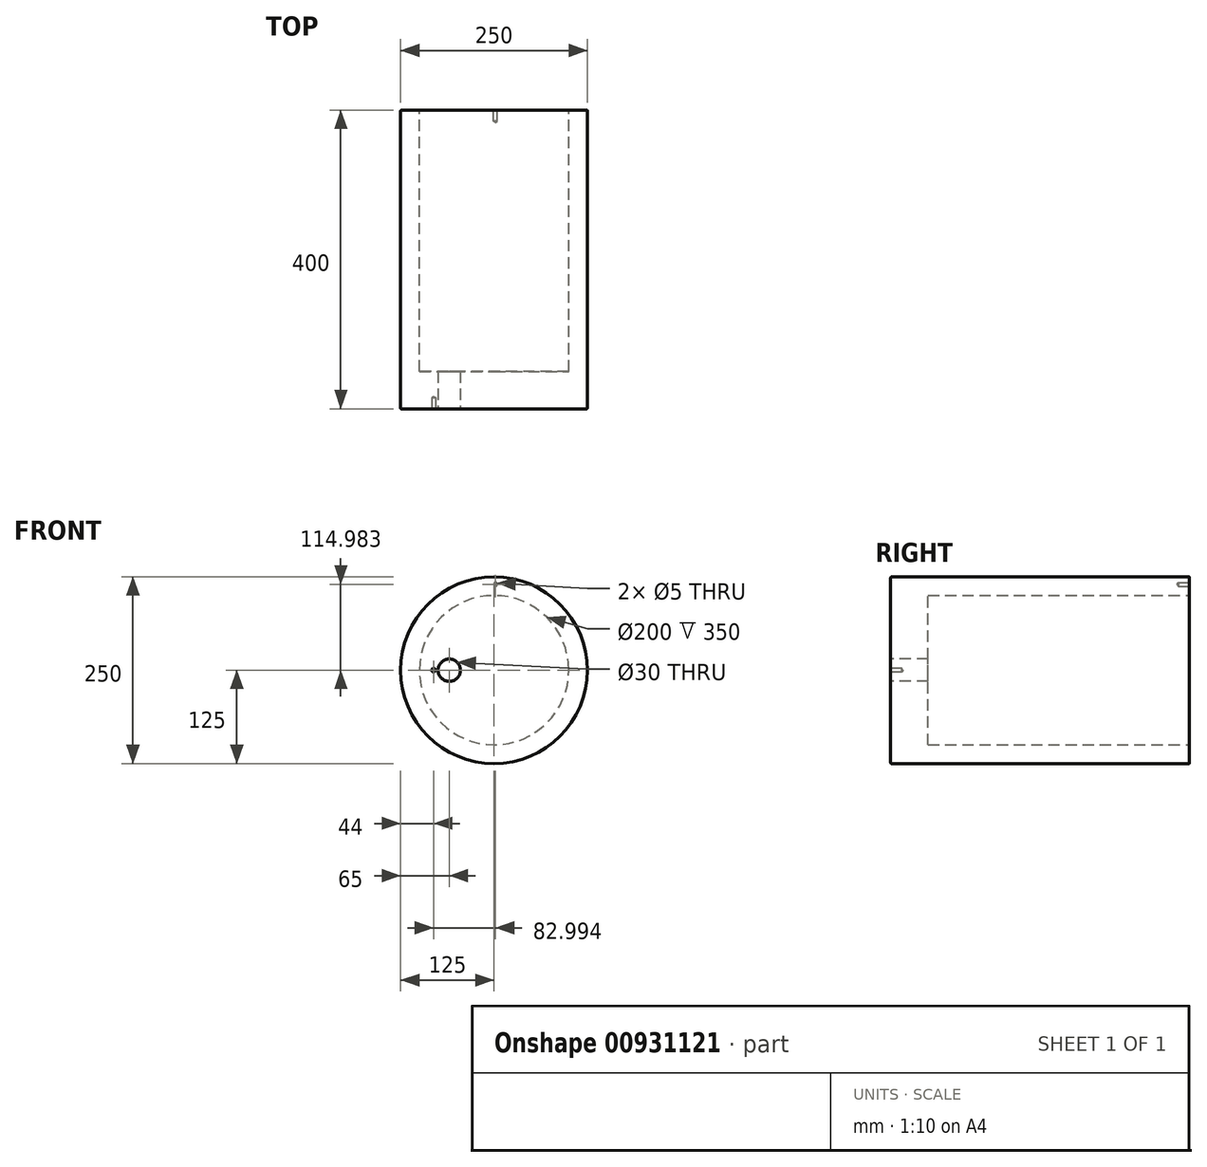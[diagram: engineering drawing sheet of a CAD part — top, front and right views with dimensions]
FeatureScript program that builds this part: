
annotation { "Feature Type Name" : "Feature", "Feature Type Description" : "" }
export const myFeature = defineFeature(function(context is Context, id is Id, definition is map)
    precondition{}
    {
        {
            var Q0;
            Q0=qCreatedBy(makeId("Front.planeOp"),FACE);
            var sketch = newSketch(context, id + "F0", { "sketchPlane" : qUnion([Q0])});
            skCircle(sketch, "E0", {"center": v(125, 0) * mm, "radius": 125 * mm});
            skSolve(sketch);
        }
        {
            var Q0;
            Q0=makeQuery(id+"F0.imprint","IMPRINT",FACE,{"disambiguationData":[TD([[makeQuery(id+"F0.imprint","IMPRINT",EDGE,{"derivedFrom":sQuery(id+"F0.wireOp",EDGE,"E0")}),1.0]])]});
            var Q1;
            Q1=sQuery(id+"F0.wireOp",EDGE,"E0");
            extrude(context, id + "F1", {"entities" : qUnion([Q0]), "surfaceEntities" : qUnion([Q1]), "depth" : 400 * mm, "offsetDistance" : 25 * mm});
        }
        {
            var Q0;
            Q0=makeQuery(id+"F0.imprint","IMPRINT",FACE,{"disambiguationData":[TD([[makeQuery(id+"F0.imprint","IMPRINT",EDGE,{"derivedFrom":sQuery(id+"F0.wireOp",EDGE,"E0")}),1.0]])]});
            var sketch = newSketch(context, id + "F2", { "sketchPlane" : qUnion([Q0])});
            skCircle(sketch, "E1", {"center": v(125, 0) * mm, "radius": 100 * mm});
            skSolve(sketch);
        }
        {
            var Q0;
            Q0=makeQuery(id+"F2.imprint","IMPRINT",FACE,{"disambiguationData":[TD([[makeQuery(id+"F2.imprint","IMPRINT",EDGE,{"derivedFrom":sQuery(id+"F2.wireOp",EDGE,"E1")}),1.0]])]});
            extrude(context, id + "F3", {"entities" : qUnion([Q0]), "operationType" : NewBodyOperationType.REMOVE, "depth" : 350 * mm, "offsetDistance" : 25 * mm});
        }
        {
            var Q0;
            Q0=makeQuery(id+"F1.opExtrude","CAP_EDGE",EDGE,{"disambiguationData":[OSD([sQuery(id+"F0.wireOp",EDGE,"E0")])],"isStart":true});
            var Q1;
            Q1=makeQuery(id+"F3.boolean.opBoolean","COPY",EDGE,{"derivedFrom":makeQuery(id+"F3.opExtrude","CAP_EDGE",EDGE,{"disambiguationData":[OSD([sQuery(id+"F2.wireOp",EDGE,"E1")])],"isStart":true})});
            var Q2;
            Q2=makeQuery(id+"F1.opExtrude","CAP_EDGE",EDGE,{"disambiguationData":[OSD([sQuery(id+"F0.wireOp",EDGE,"E0")])],"isStart":false});
            fillet(context, id + "F4", {"entities" : qUnion([Q0, Q1, Q2]), "radius" : 1 * mm, "tangentPropagation" : true, "allowEdgeOverflow" : false});
        }
        {
            var Q0;
            Q0=makeQuery(id+"F0.imprint","IMPRINT",FACE,{"disambiguationData":[TD([[makeQuery(id+"F0.imprint","IMPRINT",EDGE,{"derivedFrom":sQuery(id+"F0.wireOp",EDGE,"E0")}),1.0]])]});
            var sketch = newSketch(context, id + "F5", { "sketchPlane" : qUnion([Q0])});
            skPoint(sketch, "E2", {"position": v(127, 114.98) * mm});
            skSolve(sketch);
        }
        {
            var Q0;
            Q0=sQuery(id+"F5.wireOp",VERTEX,"E2");
            var Q1;
            Q1=makeQuery(id+"F1.opExtrude","SWEPT_BODY",BODY,{"disambiguationData":[OSD([sQuery(id+"F0.wireOp",EDGE,"E0")])]});
            hole(context, id + "F6", {"style" : HoleStyle.SIMPLE, "endStyle" : HoleEndStyle.BLIND, "oppositeDirection" : true, "standardTappedOrClearance" : lookupTablePath({ "standard" : "ISO", "engagement" : "75%", "pitch" : "1 mm", "size" : "M6", "type" : "Tapped" }), "standardBlindInLast" : lookupTablePath({ "standard" : "ISO", "fit" : "Normal", "engagement" : "75%", "pitch" : "1 mm", "size" : "M6", "type" : "Clearance & tapped" }), "holeDiameter" : 5 * mm, "majorDiameter" : 6 * mm, "showTappedDepth" : true, "holeDepth" : 15 * mm, "isTappedThrough" : true, "tappedDepth" : 12 * mm, "tapClearance" : 3, "startFromSketch" : true, "locations" : qUnion([Q0]), "scope" : qUnion([Q1])});
        }
        {
            var Q0;
            Q0=makeQuery(id+"F1.opExtrude","CAP_FACE",FACE,{"disambiguationData":[OSD([sQuery(id+"F0.wireOp",EDGE,"E0")])],"isStart":false});
            var sketch = newSketch(context, id + "F7", { "sketchPlane" : qUnion([Q0])});
            skPoint(sketch, "E3", {"position": v(65, 0) * mm});
            skSolve(sketch);
        }
        {
            var Q0;
            Q0=makeQuery(id+"F1.opExtrude","CAP_FACE",FACE,{"disambiguationData":[OSD([sQuery(id+"F0.wireOp",EDGE,"E0")])],"isStart":false});
            var sketch = newSketch(context, id + "F8", { "sketchPlane" : qUnion([Q0])});
            skPoint(sketch, "E4", {"position": v(44, 0) * mm});
            skSolve(sketch);
        }
        {
            var Q0;
            Q0=sQuery(id+"F7.wireOp",VERTEX,"E3");
            var Q1;
            Q1=makeQuery(id+"F1.opExtrude","SWEPT_BODY",BODY,{"disambiguationData":[OSD([sQuery(id+"F0.wireOp",EDGE,"E0")])]});
            hole(context, id + "F9", {"style" : HoleStyle.SIMPLE, "endStyle" : HoleEndStyle.THROUGH, "standardTappedOrClearance" : lookupTablePath({ "standard" : "ISO", "size" : "30", "type" : "Drilled" }), "standardBlindInLast" : lookupTablePath({ "standard" : "ISO", "size" : "30", "type" : "Drilled" }), "holeDiameter" : 30 * mm, "majorDiameter" : 5 * mm, "isTappedThrough" : true, "tappedDepth" : 12 * mm, "tapClearance" : 3, "startFromSketch" : true, "locations" : qUnion([Q0]), "scope" : qUnion([Q1])});
        }
        {
            var Q0;
            Q0=sQuery(id+"F8.wireOp",VERTEX,"E4");
            var Q1;
            Q1=makeQuery(id+"F1.opExtrude","SWEPT_BODY",BODY,{"disambiguationData":[OSD([sQuery(id+"F0.wireOp",EDGE,"E0")])]});
            hole(context, id + "F10", {"style" : HoleStyle.SIMPLE, "endStyle" : HoleEndStyle.BLIND, "standardTappedOrClearance" : lookupTablePath({ "standard" : "ISO", "engagement" : "75%", "pitch" : "1 mm", "size" : "M6", "type" : "Tapped" }), "standardBlindInLast" : lookupTablePath({ "standard" : "ISO", "fit" : "Normal", "engagement" : "75%", "pitch" : "1 mm", "size" : "M6", "type" : "Clearance & tapped" }), "holeDiameter" : 5 * mm, "majorDiameter" : 6 * mm, "showTappedDepth" : true, "holeDepth" : 15 * mm, "tappedDepth" : 12 * mm, "tapClearance" : 3, "startFromSketch" : true, "locations" : qUnion([Q0]), "scope" : qUnion([Q1])});
        }
    });
